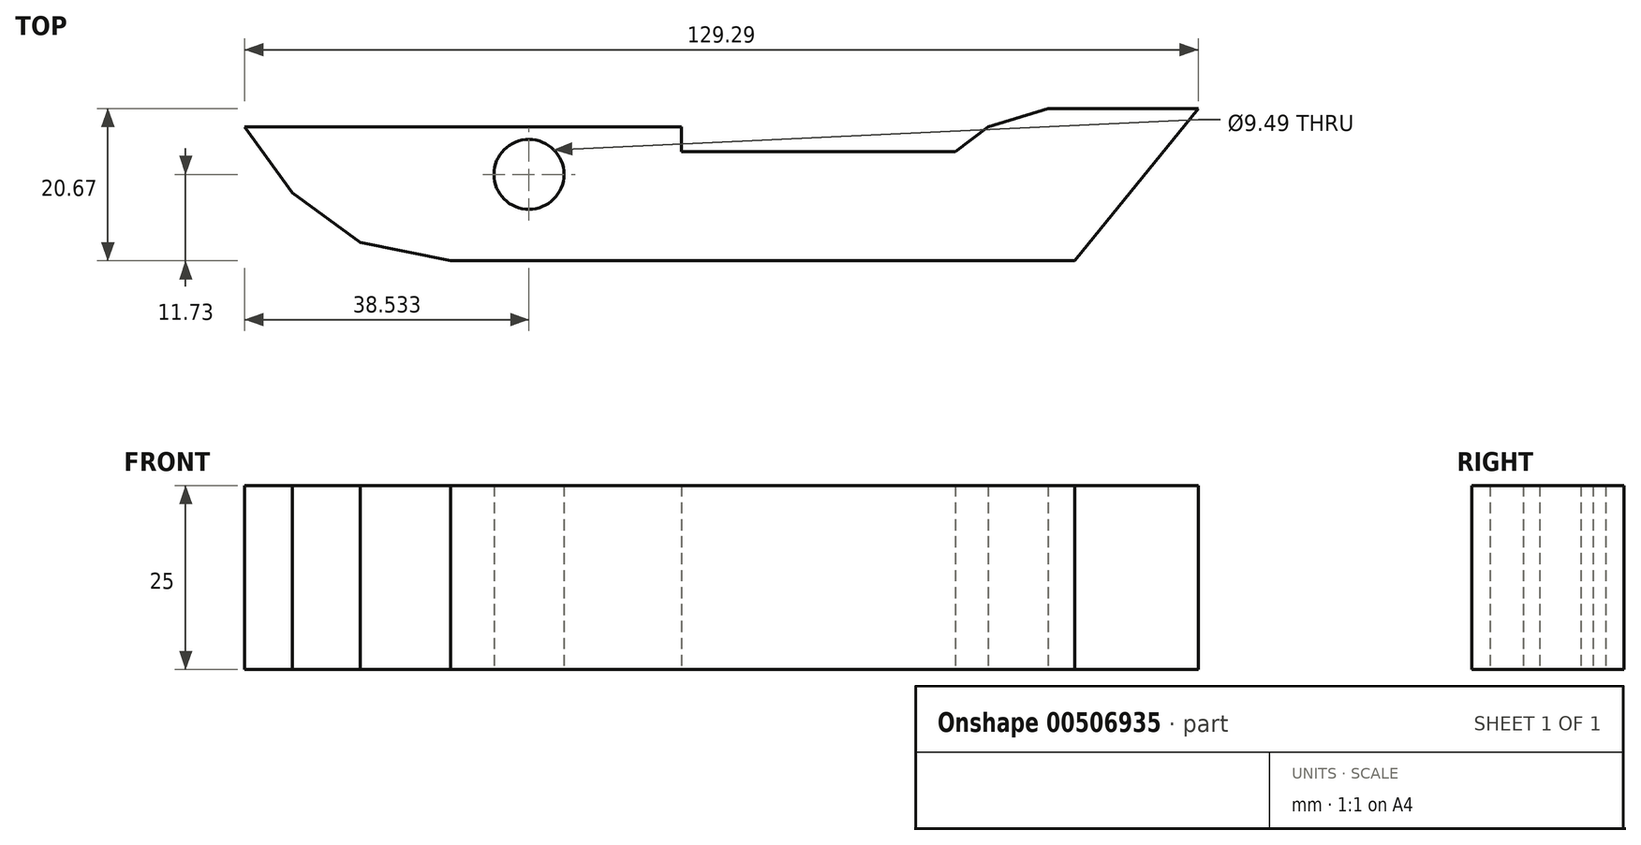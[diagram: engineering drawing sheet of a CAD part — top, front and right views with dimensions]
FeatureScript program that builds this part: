
annotation { "Feature Type Name" : "Feature", "Feature Type Description" : "" }
export const myFeature = defineFeature(function(context is Context, id is Id, definition is map)
    precondition{}
    {
        {
            var Q0;
            Q0=qCreatedBy(makeId("Top.planeOp"),FACE);
            var sketch = newSketch(context, id + "F0", { "sketchPlane" : qUnion([Q0])});
            skLineSegment(sketch, "E0", {"start": v(-23.74, -26.8) * mm, "end": v(-10.33, -26.8) * mm});
            skLineSegment(sketch, "E1", {"start": v(-10.33, -26.8) * mm, "end": v(4.47, -26.8) * mm});
            skLineSegment(sketch, "E2", {"start": v(4.47, -26.8) * mm, "end": v(22.9, -26.8) * mm});
            skLineSegment(sketch, "E3", {"start": v(22.9, -26.8) * mm, "end": v(38.54, -26.8) * mm});
            skLineSegment(sketch, "E4", {"start": v(38.54, -26.8) * mm, "end": v(50.27, -26.8) * mm});
            skLineSegment(sketch, "E5", {"start": v(50.27, -26.8) * mm, "end": v(67.02, -6.14) * mm});
            skLineSegment(sketch, "E6", {"start": v(67.02, -6.14) * mm, "end": v(46.64, -6.14) * mm});
            skLineSegment(sketch, "E7", {"start": v(46.64, -6.14) * mm, "end": v(38.54, -8.66) * mm});
            skLineSegment(sketch, "E8", {"start": v(38.54, -8.66) * mm, "end": v(34.07, -12) * mm});
            skLineSegment(sketch, "E9", {"start": v(34.07, -12) * mm, "end": v(-3.07, -12) * mm});
            skLineSegment(sketch, "E10", {"start": v(-3.07, -12) * mm, "end": v(-3.07, -8.66) * mm});
            skLineSegment(sketch, "E11", {"start": v(-3.07, -8.66) * mm, "end": v(-62.27, -8.66) * mm});
            skLineSegment(sketch, "E12", {"start": v(-62.27, -8.66) * mm, "end": v(-55.85, -17.6) * mm});
            skLineSegment(sketch, "E13", {"start": v(-55.85, -17.6) * mm, "end": v(-46.64, -24.3) * mm});
            skLineSegment(sketch, "E14", {"start": v(-46.64, -24.3) * mm, "end": v(-34.35, -26.8) * mm});
            skLineSegment(sketch, "E15", {"start": v(-34.35, -26.8) * mm, "end": v(-23.74, -26.8) * mm});
            skSolve(sketch);
        }
        {
            var Q0;
            Q0 = qSketchRegion(id + "F0", true);
            extrude(context, id + "F1", {"entities" : qUnion([Q0]), "depth" : 25 * mm});
        }
        {
            var Q0;
            Q0=qCreatedBy(makeId("Top.planeOp"),FACE);
            var sketch = newSketch(context, id + "F2", { "sketchPlane" : qUnion([Q0])});
            skCircle(sketch, "E16", {"center": v(-23.74, -15.08) * mm, "radius": 4.75 * mm});
            skSolve(sketch);
        }
        {
            var Q0;
            Q0 = qSketchRegion(id + "F2", true);
            extrude(context, id + "F3", {"entities" : qUnion([Q0]), "operationType" : NewBodyOperationType.REMOVE, "endBound" : BoundingType.THROUGH_ALL, "depth" : 25 * mm});
        }
    });
